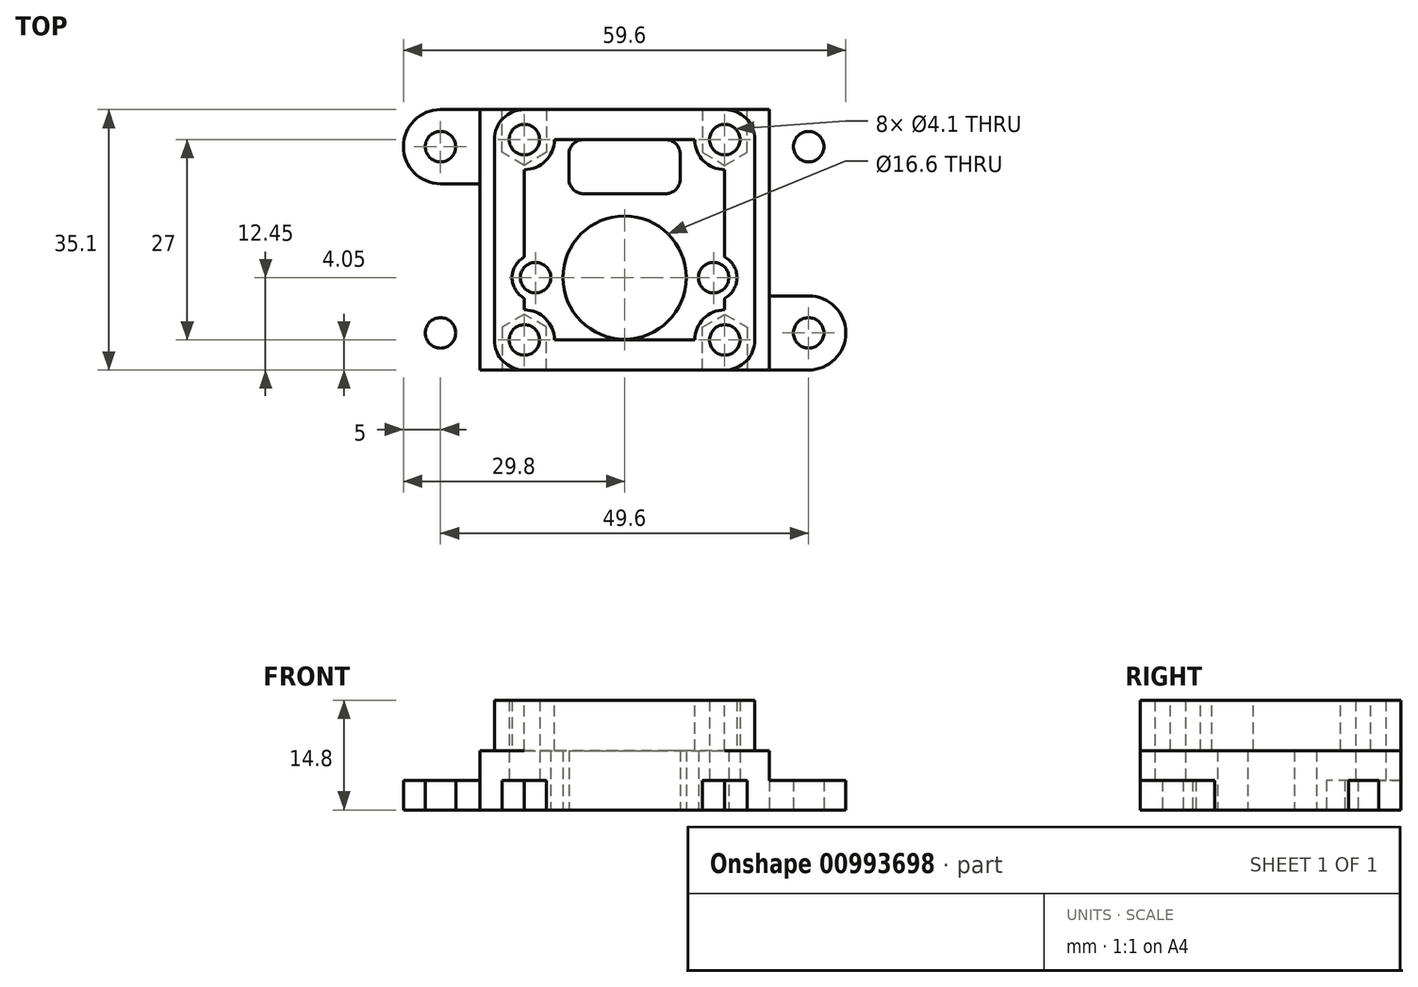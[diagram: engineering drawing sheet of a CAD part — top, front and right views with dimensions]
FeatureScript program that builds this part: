
annotation { "Feature Type Name" : "Feature", "Feature Type Description" : "" }
export const myFeature = defineFeature(function(context is Context, id is Id, definition is map)
    precondition{}
    {
        {
            var Q0;
            Q0=qCreatedBy(makeId("Top.planeOp"),FACE);
            var sketch = newSketch(context, id + "F0", { "sketchPlane" : qUnion([Q0])});
            skLineSegment(sketch, "E0.bottom", {"start": v(17.55, 17.55) * mm, "end": v(-17.55, 17.55) * mm});
            skLineSegment(sketch, "E0.top", {"start": v(17.55, -17.55) * mm, "end": v(-17.55, -17.55) * mm});
            skLineSegment(sketch, "E0.left", {"start": v(17.55, 17.55) * mm, "end": v(17.55, -17.55) * mm, "construction": true});
            skLineSegment(sketch, "E0.right", {"start": v(-17.55, 17.55) * mm, "end": v(-17.55, -17.55) * mm, "construction": true});
            skPoint(sketch, "E0.middle", {"position": v(0, 0) * mm});
            skLineSegment(sketch, "E1", {"start": v(0, 0) * mm, "end": v(0, 17.55) * mm, "construction": true});
            skLineSegment(sketch, "E2", {"start": v(0, 0) * mm, "end": v(-17.55, 0) * mm, "construction": true});
            skLineSegment(sketch, "E3.bottom", {"start": v(13.5, 13.5) * mm, "end": v(-13.5, 13.5) * mm});
            skLineSegment(sketch, "E3.top", {"start": v(13.5, -13.5) * mm, "end": v(-13.5, -13.5) * mm});
            skLineSegment(sketch, "E3.left", {"start": v(13.5, 13.5) * mm, "end": v(13.5, -13.5) * mm});
            skLineSegment(sketch, "E3.right", {"start": v(-13.5, 13.5) * mm, "end": v(-13.5, -13.5) * mm});
            skCircle(sketch, "E4", {"center": v(-13.5, 13.5) * mm, "radius": 2.05 * mm});
            skCircle(sketch, "E5", {"center": v(-13.5, 13.5) * mm, "radius": 4.05 * mm, "construction": true});
            skCircle(sketch, "E6.MirrorC", {"center": v(13.5, 13.5) * mm, "radius": 4.05 * mm, "construction": true});
            skCircle(sketch, "E7.MirrorC", {"center": v(13.5, 13.5) * mm, "radius": 2.05 * mm});
            skCircle(sketch, "E8.MirrorC", {"center": v(-13.5, -13.5) * mm, "radius": 4.05 * mm, "construction": true});
            skCircle(sketch, "E9.MirrorC", {"center": v(-13.5, -13.5) * mm, "radius": 2.05 * mm});
            skCircle(sketch, "E10.MirrorC", {"center": v(13.5, -13.5) * mm, "radius": 4.05 * mm, "construction": true});
            skCircle(sketch, "E11.MirrorC", {"center": v(13.5, -13.5) * mm, "radius": 2.05 * mm});
            skLineSegment(sketch, "E12", {"start": v(-17.55, 17.55) * mm, "end": v(-19.5, 17.55) * mm});
            skLineSegment(sketch, "E13", {"start": v(-19.5, -17.55) * mm, "end": v(-17.55, -17.55) * mm});
            skLineSegment(sketch, "E14.MirrorCS", {"start": v(17.55, 17.55) * mm, "end": v(19.5, 17.55) * mm});
            skLineSegment(sketch, "E15.MirrorCS", {"start": v(19.5, -17.55) * mm, "end": v(17.55, -17.55) * mm});
            skCircle(sketch, "E16", {"center": v(-24.8, 12.55) * mm, "radius": 2.05 * mm});
            skCircle(sketch, "E17.MirrorC", {"center": v(24.8, 12.55) * mm, "radius": 2.05 * mm});
            skCircle(sketch, "E18.MirrorC", {"center": v(-24.8, -12.55) * mm, "radius": 2.05 * mm});
            skCircle(sketch, "E19.MirrorC", {"center": v(24.8, -12.55) * mm, "radius": 2.05 * mm});
            skCircle(sketch, "E20.cCircle", {"center": v(-13.5, 13.5) * mm, "radius": 3 * mm, "construction": true});
            skLineSegment(sketch, "E20.0", {"start": v(-10.5, 15.23) * mm, "end": v(-10.5, 11.77) * mm});
            skLineSegment(sketch, "E20.1", {"start": v(-10.5, 11.77) * mm, "end": v(-13.5, 10.04) * mm});
            skLineSegment(sketch, "E20.2", {"start": v(-13.5, 10.04) * mm, "end": v(-16.5, 11.77) * mm});
            skLineSegment(sketch, "E20.3", {"start": v(-16.5, 11.77) * mm, "end": v(-16.5, 15.23) * mm});
            skLineSegment(sketch, "E20.4", {"start": v(-16.5, 15.23) * mm, "end": v(-13.5, 16.96) * mm});
            skLineSegment(sketch, "E20.5", {"start": v(-13.5, 16.96) * mm, "end": v(-10.5, 15.23) * mm});
            skPoint(sketch, "E20.0.midPoint", {"position": v(-10.5, 13.5) * mm});
            skLineSegment(sketch, "E21.MirrorCS", {"start": v(10.5, 15.23) * mm, "end": v(10.5, 11.77) * mm});
            skLineSegment(sketch, "E22.MirrorCS", {"start": v(13.5, 16.96) * mm, "end": v(10.5, 15.23) * mm});
            skLineSegment(sketch, "E23.MirrorCS", {"start": v(16.5, 15.23) * mm, "end": v(13.5, 16.96) * mm});
            skLineSegment(sketch, "E24.MirrorCS", {"start": v(16.5, 11.77) * mm, "end": v(16.5, 15.23) * mm});
            skLineSegment(sketch, "E25.MirrorCS", {"start": v(13.5, 10.04) * mm, "end": v(16.5, 11.77) * mm});
            skLineSegment(sketch, "E26.MirrorCS", {"start": v(10.5, 11.77) * mm, "end": v(13.5, 10.04) * mm});
            skLineSegment(sketch, "E27.MirrorCS", {"start": v(-10.5, -11.77) * mm, "end": v(-13.5, -10.04) * mm});
            skLineSegment(sketch, "E28.MirrorCS", {"start": v(-10.5, -15.23) * mm, "end": v(-10.5, -11.77) * mm});
            skLineSegment(sketch, "E29.MirrorCS", {"start": v(-13.5, -16.96) * mm, "end": v(-10.5, -15.23) * mm});
            skLineSegment(sketch, "E30.MirrorCS", {"start": v(-16.5, -15.23) * mm, "end": v(-13.5, -16.96) * mm});
            skLineSegment(sketch, "E31.MirrorCS", {"start": v(-16.5, -11.77) * mm, "end": v(-16.5, -15.23) * mm});
            skLineSegment(sketch, "E32.MirrorCS", {"start": v(-13.5, -10.04) * mm, "end": v(-16.5, -11.77) * mm});
            skLineSegment(sketch, "E33.MirrorCS", {"start": v(10.5, -11.77) * mm, "end": v(13.5, -10.04) * mm});
            skLineSegment(sketch, "E34.MirrorCS", {"start": v(10.5, -15.23) * mm, "end": v(10.5, -11.77) * mm});
            skLineSegment(sketch, "E35.MirrorCS", {"start": v(13.5, -16.96) * mm, "end": v(10.5, -15.23) * mm});
            skLineSegment(sketch, "E36.MirrorCS", {"start": v(16.5, -15.23) * mm, "end": v(13.5, -16.96) * mm});
            skLineSegment(sketch, "E37.MirrorCS", {"start": v(16.5, -11.77) * mm, "end": v(16.5, -15.23) * mm});
            skLineSegment(sketch, "E38.MirrorCS", {"start": v(13.5, -10.04) * mm, "end": v(16.5, -11.77) * mm});
            skLineSegment(sketch, "E39", {"start": v(-16.5, 15.23) * mm, "end": v(-16.5, 17.55) * mm});
            skLineSegment(sketch, "E40", {"start": v(-10.5, 15.23) * mm, "end": v(-10.5, 17.55) * mm});
            skLineSegment(sketch, "E41", {"start": v(10.5, 15.23) * mm, "end": v(10.5, 17.55) * mm});
            skLineSegment(sketch, "E42", {"start": v(16.5, 15.23) * mm, "end": v(16.5, 17.55) * mm});
            skLineSegment(sketch, "E43", {"start": v(16.5, -15.23) * mm, "end": v(16.5, -17.55) * mm});
            skLineSegment(sketch, "E44", {"start": v(10.5, -15.23) * mm, "end": v(10.5, -17.55) * mm});
            skLineSegment(sketch, "E45", {"start": v(-10.5, -15.23) * mm, "end": v(-10.5, -17.55) * mm});
            skLineSegment(sketch, "E46", {"start": v(-16.5, -15.23) * mm, "end": v(-16.5, -17.55) * mm});
            skLineSegment(sketch, "E47", {"start": v(-19.5, 17.55) * mm, "end": v(-19.5, -17.55) * mm});
            skLineSegment(sketch, "E48", {"start": v(19.5, 17.55) * mm, "end": v(19.5, -17.55) * mm});
            skCircle(sketch, "E49", {"center": v(0, -5.1) * mm, "radius": 8.3 * mm});
            skCircle(sketch, "E50", {"center": v(-12, -5.1) * mm, "radius": 2.05 * mm});
            skCircle(sketch, "E51", {"center": v(-12, -5.1) * mm, "radius": 3.15 * mm});
            skLineSegment(sketch, "E52", {"start": v(-13.5, -5.1) * mm, "end": v(13.5, -5.1) * mm, "construction": true});
            skLineSegment(sketch, "E53.bottom", {"start": v(-5.5, 13.5) * mm, "end": v(5.5, 13.5) * mm});
            skLineSegment(sketch, "E53.top", {"start": v(-5.5, 6.2) * mm, "end": v(5.5, 6.2) * mm});
            skLineSegment(sketch, "E53.left", {"start": v(-7.5, 11.5) * mm, "end": v(-7.5, 8.2) * mm});
            skLineSegment(sketch, "E53.right", {"start": v(7.5, 11.5) * mm, "end": v(7.5, 8.2) * mm});
            skPoint(sketch, "E53.middle", {"position": v(0, 9.85) * mm});
            skPoint(sketch, "E54.visualSharp", {"position": v(-7.5, 6.2) * mm});
            skArc(sketch, "E54.filletArc", {"start": v(-7.5, 8.2) * mm, "mid": v(-6.91, 6.79) * mm, "end": v(-5.5, 6.2) * mm});
            skPoint(sketch, "E55.visualSharp", {"position": v(7.5, 6.2) * mm});
            skArc(sketch, "E55.filletArc", {"start": v(5.5, 6.2) * mm, "mid": v(6.91, 6.79) * mm, "end": v(7.5, 8.2) * mm});
            skPoint(sketch, "E56.visualSharp", {"position": v(7.5, 13.5) * mm});
            skArc(sketch, "E56.filletArc", {"start": v(7.5, 11.5) * mm, "mid": v(6.91, 12.91) * mm, "end": v(5.5, 13.5) * mm});
            skPoint(sketch, "E57.visualSharp", {"position": v(-7.5, 13.5) * mm});
            skArc(sketch, "E57.filletArc", {"start": v(-5.5, 13.5) * mm, "mid": v(-6.91, 12.91) * mm, "end": v(-7.5, 11.5) * mm});
            skArc(sketch, "E58", {"start": v(-24.8, 17.55) * mm, "mid": v(-29.8, 12.55) * mm, "end": v(-24.8, 7.55) * mm});
            skArc(sketch, "E59", {"start": v(-24.8, -7.55) * mm, "mid": v(-29.8, -12.55) * mm, "end": v(-24.8, -17.55) * mm});
            skLineSegment(sketch, "E60", {"start": v(-24.8, 17.55) * mm, "end": v(-19.5, 17.55) * mm});
            skLineSegment(sketch, "E61", {"start": v(-24.8, 7.55) * mm, "end": v(-19.5, 7.55) * mm});
            skLineSegment(sketch, "E62.MirrorCS", {"start": v(24.8, 7.55) * mm, "end": v(19.5, 7.55) * mm});
            skArc(sketch, "E63.MirrorCS", {"start": v(24.8, 17.55) * mm, "mid": v(29.8, 12.55) * mm, "end": v(24.8, 7.55) * mm});
            skLineSegment(sketch, "E64.MirrorCS", {"start": v(24.8, 17.55) * mm, "end": v(19.5, 17.55) * mm});
            skLineSegment(sketch, "E65.MirrorCS", {"start": v(-24.8, -7.55) * mm, "end": v(-19.5, -7.55) * mm});
            skArc(sketch, "E66.MirrorCS", {"start": v(-24.8, -17.55) * mm, "mid": v(-29.8, -12.55) * mm, "end": v(-24.8, -7.55) * mm});
            skLineSegment(sketch, "E67.MirrorCS", {"start": v(-24.8, -17.55) * mm, "end": v(-19.5, -17.55) * mm});
            skLineSegment(sketch, "E68.MirrorCS", {"start": v(24.8, -17.55) * mm, "end": v(19.5, -17.55) * mm});
            skArc(sketch, "E69.MirrorCS", {"start": v(24.8, -17.55) * mm, "mid": v(29.8, -12.55) * mm, "end": v(24.8, -7.55) * mm});
            skLineSegment(sketch, "E70.MirrorCS", {"start": v(24.8, -7.55) * mm, "end": v(19.5, -7.55) * mm});
            skCircle(sketch, "E71.MirrorC", {"center": v(12, -5.1) * mm, "radius": 3.15 * mm});
            skCircle(sketch, "E72.MirrorC", {"center": v(12, -5.1) * mm, "radius": 2.05 * mm});
            skSolve(sketch);
        }
        {
            var Q0;
            {var subQ1=sQuery(id+"F0.wireOp",EDGE,"E20.2");Q0=makeQuery(id+"F0.imprint","IMPRINT",FACE,{"disambiguationData":[TD([[makeQuery(id+"F0.imprint","IMPRINT",EDGE,{"derivedFrom":subQ1}),1.0]])]});}
            var Q1;
            {var subQ1=sQuery(id+"F0.wireOp",EDGE,"E20.1");Q1=makeQuery(id+"F0.imprint","IMPRINT",FACE,{"disambiguationData":[TD([[makeQuery(id+"F0.imprint","IMPRINT",EDGE,{"derivedFrom":subQ1}),1.0]])]});}
            var Q2;
            {var subQ0=sQuery(id+"F0.wireOp",EDGE,"E40");Q2=makeQuery(id+"F0.imprint","IMPRINT",FACE,{"disambiguationData":[TD([[makeQuery(id+"F0.imprint","IMPRINT",EDGE,{"derivedFrom":subQ0}),-1.0]])]});}
            var Q3;
            Q3=makeQuery(id+"F0.imprint","IMPRINT",FACE,{"disambiguationData":[TD([[makeQuery(id+"F0.imprint","IMPRINT",EDGE,{"derivedFrom":sQuery(id+"F0.wireOp",EDGE,"E24.MirrorCS")}),-1.0]])]});
            var Q4;
            {var subQ7=sQuery(id+"F0.wireOp",EDGE,"E44");Q4=makeQuery(id+"F0.imprint","IMPRINT",FACE,{"disambiguationData":[TD([[makeQuery(id+"F0.imprint","IMPRINT",EDGE,{"derivedFrom":subQ7}),-1.0]])]});}
            var Q5;
            Q5=makeQuery(id+"F0.imprint","IMPRINT",FACE,{"disambiguationData":[TD([[makeQuery(id+"F0.imprint","IMPRINT",EDGE,{"derivedFrom":sQuery(id+"F0.wireOp",EDGE,"E20.4")}),1.0]])]});
            var Q6;
            {var subQ8=sQuery(id+"F0.wireOp",EDGE,"E20.2");Q6=makeQuery(id+"F0.imprint","IMPRINT",FACE,{"disambiguationData":[TD([[makeQuery(id+"F0.imprint","IMPRINT",EDGE,{"derivedFrom":subQ8}),-1.0]])]});}
            var Q7;
            Q7=makeQuery(id+"F0.imprint","IMPRINT",FACE,{"disambiguationData":[TD([[makeQuery(id+"F0.imprint","IMPRINT",EDGE,{"derivedFrom":sQuery(id+"F0.wireOp",EDGE,"E22.MirrorCS")}),-1.0]])]});
            var Q8;
            {var subQ6=sQuery(id+"F0.wireOp",EDGE,"E22.MirrorCS");Q8=makeQuery(id+"F0.imprint","IMPRINT",FACE,{"disambiguationData":[TD([[makeQuery(id+"F0.imprint","IMPRINT",EDGE,{"derivedFrom":subQ6}),1.0]])]});}
            var Q9;
            {var subQ0=sQuery(id+"F0.wireOp",EDGE,"E26.MirrorCS");Q9=makeQuery(id+"F0.imprint","IMPRINT",FACE,{"disambiguationData":[TD([[makeQuery(id+"F0.imprint","IMPRINT",EDGE,{"derivedFrom":subQ0}),1.0]])]});}
            var Q10;
            {var subQ0=sQuery(id+"F0.wireOp",EDGE,"E20.1");Q10=makeQuery(id+"F0.imprint","IMPRINT",FACE,{"disambiguationData":[TD([[makeQuery(id+"F0.imprint","IMPRINT",EDGE,{"derivedFrom":subQ0}),-1.0]])]});}
            var Q11;
            {var subQ5=sQuery(id+"F0.wireOp",EDGE,"E27.MirrorCS");Q11=makeQuery(id+"F0.imprint","IMPRINT",FACE,{"disambiguationData":[TD([[makeQuery(id+"F0.imprint","IMPRINT",EDGE,{"derivedFrom":subQ5}),1.0]])]});}
            var Q12;
            {var subQ0=sQuery(id+"F0.wireOp",EDGE,"E29.MirrorCS");Q12=makeQuery(id+"F0.imprint","IMPRINT",FACE,{"disambiguationData":[TD([[makeQuery(id+"F0.imprint","IMPRINT",EDGE,{"derivedFrom":subQ0}),1.0]])]});}
            var Q13;
            Q13=makeQuery(id+"F0.imprint","IMPRINT",FACE,{"disambiguationData":[TD([[makeQuery(id+"F0.imprint","IMPRINT",EDGE,{"derivedFrom":sQuery(id+"F0.wireOp",EDGE,"E29.MirrorCS")}),-1.0]])]});
            var Q14;
            Q14=makeQuery(id+"F0.imprint","IMPRINT",FACE,{"disambiguationData":[TD([[makeQuery(id+"F0.imprint","IMPRINT",EDGE,{"derivedFrom":sQuery(id+"F0.wireOp",EDGE,"E35.MirrorCS")}),1.0]])]});
            var Q15;
            {var subQ0=sQuery(id+"F0.wireOp",EDGE,"E35.MirrorCS");Q15=makeQuery(id+"F0.imprint","IMPRINT",FACE,{"disambiguationData":[TD([[makeQuery(id+"F0.imprint","IMPRINT",EDGE,{"derivedFrom":subQ0}),-1.0]])]});}
            var Q16;
            {var subQ7=sQuery(id+"F0.wireOp",EDGE,"E33.MirrorCS");Q16=makeQuery(id+"F0.imprint","IMPRINT",FACE,{"disambiguationData":[TD([[makeQuery(id+"F0.imprint","IMPRINT",EDGE,{"derivedFrom":subQ7}),-1.0]])]});}
            var Q17;
            Q17=makeQuery(id+"F0.imprint","IMPRINT",FACE,{"disambiguationData":[TD([[makeQuery(id+"F0.imprint","IMPRINT",EDGE,{"derivedFrom":sQuery(id+"F0.wireOp",EDGE,"nuV7RpCx-R8Kc-sA3T-knKH-8SdXEwqvr1Y3")}),1.0]])]});
            var Q18;
            Q18=makeQuery(id+"F0.imprint","IMPRINT",FACE,{"disambiguationData":[TD([[makeQuery(id+"F0.imprint","IMPRINT",EDGE,{"derivedFrom":sQuery(id+"F0.wireOp",EDGE,"B5VoDuBN-S8xL-bz7c-algA-acrGaq53pSVS")}),1.0]])]});
            var Q19;
            {var subQ7=sQuery(id+"F0.wireOp",EDGE,"B5VoDuBN-S8xL-bz7c-algA-acrGaq53pSVS");Q19=makeQuery(id+"F0.imprint","IMPRINT",FACE,{"disambiguationData":[TD([[makeQuery(id+"F0.imprint","IMPRINT",EDGE,{"derivedFrom":subQ7}),-1.0]])]});}
            var Q20;
            {var subQ0=sQuery(id+"F0.wireOp",EDGE,"E26.MirrorCS");Q20=makeQuery(id+"F0.imprint","IMPRINT",FACE,{"disambiguationData":[TD([[makeQuery(id+"F0.imprint","IMPRINT",EDGE,{"derivedFrom":subQ0}),-1.0]])]});}
            var Q21;
            Q21=makeQuery(id+"F0.imprint","IMPRINT",FACE,{"disambiguationData":[TD([[makeQuery(id+"F0.imprint","IMPRINT",EDGE,{"derivedFrom":sQuery(id+"F0.wireOp",EDGE,"8ItnjwQV-7nQZ-PuKx-0Jwr-2TPdBdbSkfHZ")}),-1.0]])]});
            var Q22;
            Q22=makeQuery(id+"F0.imprint","IMPRINT",FACE,{"disambiguationData":[TD([[makeQuery(id+"F0.imprint","IMPRINT",EDGE,{"derivedFrom":sQuery(id+"F0.wireOp",EDGE,"8adYv2pj-t3p7-Cn0L-WwMu-koROzQhryOGd")}),-1.0]])]});
            var Q23;
            {var subQ0=sQuery(id+"F0.wireOp",EDGE,"wJV0zkYp-PxIc-I7u3-SHVp-S6dmDnbKQt5D");var subQ1=sQuery(id+"F0.wireOp",EDGE,"E3.left");var subQ2=makeQuery(id+"F0.imprint","INTERSECT",VERTEX,{"disambiguationData":[OD(0.0)],"derivedFrom":[subQ1,subQ0]});Q23=makeQuery(id+"F0.imprint","IMPRINT",FACE,{"disambiguationData":[TD([[makeQuery(id+"F0.imprint","IMPRINT",EDGE,{"disambiguationData":[TD([[subQ2,-1.0]])],"derivedFrom":subQ1}),1.0]])]});}
            var Q24;
            Q24=makeQuery(id+"F0.imprint","IMPRINT",FACE,{"disambiguationData":[TD([[makeQuery(id+"F0.imprint","IMPRINT",EDGE,{"derivedFrom":sQuery(id+"F0.wireOp",EDGE,"8ItnjwQV-7nQZ-PuKx-0Jwr-2TPdBdbSkfHZ")}),1.0]])]});
            var Q25;
            {var subQ0=sQuery(id+"F0.wireOp",EDGE,"YWPBbz1K-cqDX-BCyH-acbg-6dvT2AnOIS1P");var subQ1=sQuery(id+"F0.wireOp",EDGE,"E3.right");var subQ2=makeQuery(id+"F0.imprint","INTERSECT",VERTEX,{"disambiguationData":[OD(0.0)],"derivedFrom":[subQ1,subQ0]});Q25=makeQuery(id+"F0.imprint","IMPRINT",FACE,{"disambiguationData":[TD([[makeQuery(id+"F0.imprint","IMPRINT",EDGE,{"disambiguationData":[TD([[subQ2,-1.0]])],"derivedFrom":subQ1}),-1.0]])]});}
            var Q26;
            Q26=makeQuery(id+"F0.imprint","IMPRINT",FACE,{"disambiguationData":[TD([[makeQuery(id+"F0.imprint","IMPRINT",EDGE,{"derivedFrom":sQuery(id+"F0.wireOp",EDGE,"8adYv2pj-t3p7-Cn0L-WwMu-koROzQhryOGd")}),1.0]])]});
            extrude(context, id + "F1", {"entities" : qUnion([Q0, Q1, Q2, Q3, Q4, Q5, Q6, Q7, Q8, Q9, Q10, Q11, Q12, Q13, Q14, Q15, Q16, Q17, Q18, Q19, Q20, Q21, Q22, Q23, Q24, Q25, Q26]), "depth" : 14.8 * mm, "offsetDistance" : 25 * mm});
        }
        {
            var Q0;
            Q0=makeQuery(id+"F0.imprint","IMPRINT",FACE,{"disambiguationData":[TD([[makeQuery(id+"F0.imprint","IMPRINT",EDGE,{"derivedFrom":sQuery(id+"F0.wireOp",EDGE,"E16")}),-1.0]])]});
            var Q1;
            Q1=makeQuery(id+"F0.imprint","IMPRINT",FACE,{"disambiguationData":[TD([[makeQuery(id+"F0.imprint","IMPRINT",EDGE,{"derivedFrom":sQuery(id+"F0.wireOp",EDGE,"E18.MirrorC")}),1.0]])]});
            var Q2;
            Q2=makeQuery(id+"F0.imprint","IMPRINT",FACE,{"disambiguationData":[TD([[makeQuery(id+"F0.imprint","IMPRINT",EDGE,{"derivedFrom":sQuery(id+"F0.wireOp",EDGE,"E19.MirrorC")}),-1.0]])]});
            var Q3;
            Q3=makeQuery(id+"F0.imprint","IMPRINT",FACE,{"disambiguationData":[TD([[makeQuery(id+"F0.imprint","IMPRINT",EDGE,{"derivedFrom":sQuery(id+"F0.wireOp",EDGE,"E17.MirrorC")}),1.0]])]});
            extrude(context, id + "F2", {"entities" : qUnion([Q0, Q1, Q2, Q3]), "operationType" : NewBodyOperationType.ADD, "depth" : 4 * mm, "offsetDistance" : 25 * mm});
        }
        {
            var Q0;
            {var subQ6=sQuery(id+"F0.wireOp",EDGE,"E22.MirrorCS");Q0=makeQuery(id+"F0.imprint","IMPRINT",FACE,{"disambiguationData":[TD([[makeQuery(id+"F0.imprint","IMPRINT",EDGE,{"derivedFrom":subQ6}),1.0]])]});}
            var Q1;
            {var subQ0=sQuery(id+"F0.wireOp",EDGE,"E26.MirrorCS");Q1=makeQuery(id+"F0.imprint","IMPRINT",FACE,{"disambiguationData":[TD([[makeQuery(id+"F0.imprint","IMPRINT",EDGE,{"derivedFrom":subQ0}),1.0]])]});}
            var Q2;
            Q2=makeQuery(id+"F0.imprint","IMPRINT",FACE,{"disambiguationData":[TD([[makeQuery(id+"F0.imprint","IMPRINT",EDGE,{"derivedFrom":sQuery(id+"F0.wireOp",EDGE,"E22.MirrorCS")}),-1.0]])]});
            var Q3;
            {var subQ8=sQuery(id+"F0.wireOp",EDGE,"E20.2");Q3=makeQuery(id+"F0.imprint","IMPRINT",FACE,{"disambiguationData":[TD([[makeQuery(id+"F0.imprint","IMPRINT",EDGE,{"derivedFrom":subQ8}),-1.0]])]});}
            var Q4;
            {var subQ0=sQuery(id+"F0.wireOp",EDGE,"E20.1");Q4=makeQuery(id+"F0.imprint","IMPRINT",FACE,{"disambiguationData":[TD([[makeQuery(id+"F0.imprint","IMPRINT",EDGE,{"derivedFrom":subQ0}),-1.0]])]});}
            var Q5;
            Q5=makeQuery(id+"F0.imprint","IMPRINT",FACE,{"disambiguationData":[TD([[makeQuery(id+"F0.imprint","IMPRINT",EDGE,{"derivedFrom":sQuery(id+"F0.wireOp",EDGE,"E20.4")}),1.0]])]});
            var Q6;
            {var subQ7=sQuery(id+"F0.wireOp",EDGE,"E33.MirrorCS");Q6=makeQuery(id+"F0.imprint","IMPRINT",FACE,{"disambiguationData":[TD([[makeQuery(id+"F0.imprint","IMPRINT",EDGE,{"derivedFrom":subQ7}),-1.0]])]});}
            var Q7;
            {var subQ0=sQuery(id+"F0.wireOp",EDGE,"E35.MirrorCS");Q7=makeQuery(id+"F0.imprint","IMPRINT",FACE,{"disambiguationData":[TD([[makeQuery(id+"F0.imprint","IMPRINT",EDGE,{"derivedFrom":subQ0}),-1.0]])]});}
            var Q8;
            Q8=makeQuery(id+"F0.imprint","IMPRINT",FACE,{"disambiguationData":[TD([[makeQuery(id+"F0.imprint","IMPRINT",EDGE,{"derivedFrom":sQuery(id+"F0.wireOp",EDGE,"E35.MirrorCS")}),1.0]])]});
            var Q9;
            {var subQ0=sQuery(id+"F0.wireOp",EDGE,"E29.MirrorCS");Q9=makeQuery(id+"F0.imprint","IMPRINT",FACE,{"disambiguationData":[TD([[makeQuery(id+"F0.imprint","IMPRINT",EDGE,{"derivedFrom":subQ0}),1.0]])]});}
            var Q10;
            {var subQ5=sQuery(id+"F0.wireOp",EDGE,"E27.MirrorCS");Q10=makeQuery(id+"F0.imprint","IMPRINT",FACE,{"disambiguationData":[TD([[makeQuery(id+"F0.imprint","IMPRINT",EDGE,{"derivedFrom":subQ5}),1.0]])]});}
            var Q11;
            Q11=makeQuery(id+"F0.imprint","IMPRINT",FACE,{"disambiguationData":[TD([[makeQuery(id+"F0.imprint","IMPRINT",EDGE,{"derivedFrom":sQuery(id+"F0.wireOp",EDGE,"E29.MirrorCS")}),-1.0]])]});
            extrude(context, id + "F3", {"entities" : qUnion([Q0, Q1, Q2, Q3, Q4, Q5, Q6, Q7, Q8, Q9, Q10, Q11]), "operationType" : NewBodyOperationType.REMOVE, "depth" : 4 * mm, "offsetDistance" : 25 * mm});
        }
        {
            var Q0;
            Q0=makeQuery(id+"F1.opExtrude","CAP_FACE",FACE,{"disambiguationData":[OSD([sQuery(id+"F0.wireOp",EDGE,"E0.bottom"),sQuery(id+"F0.wireOp",EDGE,"E0.top"),sQuery(id+"F0.wireOp",EDGE,"E4"),sQuery(id+"F0.wireOp",EDGE,"E7.MirrorC"),sQuery(id+"F0.wireOp",EDGE,"E9.MirrorC"),sQuery(id+"F0.wireOp",EDGE,"E11.MirrorC"),sQuery(id+"F0.wireOp",EDGE,"E12"),sQuery(id+"F0.wireOp",EDGE,"E13"),sQuery(id+"F0.wireOp",EDGE,"E14.MirrorCS"),sQuery(id+"F0.wireOp",EDGE,"E15.MirrorCS"),sQuery(id+"F0.wireOp",EDGE,"nuV7RpCx-R8Kc-sA3T-knKH-8SdXEwqvr1Y3"),sQuery(id+"F0.wireOp",EDGE,"B5VoDuBN-S8xL-bz7c-algA-acrGaq53pSVS"),sQuery(id+"F0.wireOp",EDGE,"E47"),sQuery(id+"F0.wireOp",EDGE,"E48")])],"isStart":false});
            var sketch = newSketch(context, id + "F4", { "sketchPlane" : qUnion([Q0])});
            skCircle(sketch, "E73.0", {"center": v(13.5, 13.5) * mm, "radius": 2.05 * mm});
            skCircle(sketch, "E73.1", {"center": v(13.5, -13.5) * mm, "radius": 2.05 * mm});
            skCircle(sketch, "E73.2", {"center": v(-13.5, -13.5) * mm, "radius": 2.05 * mm});
            skCircle(sketch, "E73.3", {"center": v(-13.5, 13.5) * mm, "radius": 2.05 * mm});
            skLineSegment(sketch, "E74", {"start": v(13.5, 13.5) * mm, "end": v(-13.5, 13.5) * mm});
            skLineSegment(sketch, "E75", {"start": v(-13.5, -13.5) * mm, "end": v(-13.5, 13.5) * mm});
            skLineSegment(sketch, "E76", {"start": v(-13.5, -13.5) * mm, "end": v(13.5, -13.5) * mm});
            skLineSegment(sketch, "E77", {"start": v(13.5, -13.5) * mm, "end": v(13.5, 13.5) * mm});
            skLineSegment(sketch, "E78.0", {"start": v(19.5, 17.55) * mm, "end": v(-19.5, 17.55) * mm});
            skLineSegment(sketch, "E79.0", {"start": v(-19.5, -17.55) * mm, "end": v(19.5, -17.55) * mm});
            skCircle(sketch, "E80", {"center": v(-13.5, 13.5) * mm, "radius": 4.05 * mm});
            skCircle(sketch, "E81", {"center": v(13.5, 13.5) * mm, "radius": 4.05 * mm});
            skCircle(sketch, "E82", {"center": v(-13.5, -13.5) * mm, "radius": 4.05 * mm});
            skCircle(sketch, "E83", {"center": v(13.5, -13.5) * mm, "radius": 4.05 * mm});
            skLineSegment(sketch, "E84", {"start": v(17.55, -17.55) * mm, "end": v(17.55, 17.55) * mm});
            skLineSegment(sketch, "E85", {"start": v(-17.55, -17.55) * mm, "end": v(-17.55, 17.55) * mm});
            skSolve(sketch);
        }
        {
            var Q0;
            {var subQ0=sQuery(id+"F4.wireOp",EDGE,"E85");var subQ1=sQuery(id+"F4.wireOp",EDGE,"E79.0");var subQ2=makeQuery(id+"F4.imprint","INTERSECT",VERTEX,{"derivedFrom":[subQ1,subQ0]});Q0=makeQuery(id+"F4.imprint","IMPRINT",FACE,{"disambiguationData":[TD([[makeQuery(id+"F4.imprint","IMPRINT",EDGE,{"disambiguationData":[TD([[subQ2,-1.0]])],"derivedFrom":subQ1}),1.0]])]});}
            var Q1;
            {var subQ4=makeQuery(id+"F1.opExtrude","CAP_EDGE",EDGE,{"disambiguationData":[OSD([sQuery(id+"F0.wireOp",EDGE,"E47")])],"isStart":false});Q1=makeQuery(id+"F4.imprint","IMPRINT",FACE,{"disambiguationData":[TD([[makeQuery(id+"F4.imprint","IMPRINT",EDGE,{"derivedFrom":subQ4}),1.0]])]});}
            var Q2;
            {var subQ0=sQuery(id+"F4.wireOp",EDGE,"E85");var subQ1=sQuery(id+"F4.wireOp",EDGE,"E78.0");var subQ2=makeQuery(id+"F4.imprint","INTERSECT",VERTEX,{"derivedFrom":[subQ1,subQ0]});Q2=makeQuery(id+"F4.imprint","IMPRINT",FACE,{"disambiguationData":[TD([[makeQuery(id+"F4.imprint","IMPRINT",EDGE,{"disambiguationData":[TD([[subQ2,1.0]])],"derivedFrom":subQ1}),1.0]])]});}
            var Q3;
            {var subQ0=sQuery(id+"F4.wireOp",EDGE,"E84");var subQ1=sQuery(id+"F4.wireOp",EDGE,"E78.0");var subQ2=makeQuery(id+"F4.imprint","INTERSECT",VERTEX,{"derivedFrom":[subQ1,subQ0]});Q3=makeQuery(id+"F4.imprint","IMPRINT",FACE,{"disambiguationData":[TD([[makeQuery(id+"F4.imprint","IMPRINT",EDGE,{"disambiguationData":[TD([[subQ2,-1.0]])],"derivedFrom":subQ1}),1.0]])]});}
            var Q4;
            {var subQ5=makeQuery(id+"F1.opExtrude","CAP_EDGE",EDGE,{"disambiguationData":[OSD([sQuery(id+"F0.wireOp",EDGE,"E48")])],"isStart":false});Q4=makeQuery(id+"F4.imprint","IMPRINT",FACE,{"disambiguationData":[TD([[makeQuery(id+"F4.imprint","IMPRINT",EDGE,{"derivedFrom":subQ5}),-1.0]])]});}
            var Q5;
            {var subQ0=sQuery(id+"F4.wireOp",EDGE,"E84");var subQ1=sQuery(id+"F4.wireOp",EDGE,"E79.0");var subQ2=makeQuery(id+"F4.imprint","INTERSECT",VERTEX,{"derivedFrom":[subQ1,subQ0]});Q5=makeQuery(id+"F4.imprint","IMPRINT",FACE,{"disambiguationData":[TD([[makeQuery(id+"F4.imprint","IMPRINT",EDGE,{"disambiguationData":[TD([[subQ2,1.0]])],"derivedFrom":subQ1}),1.0]])]});}
            var Q6;
            Q6=makeQuery(id+"F4.imprint","IMPRINT",FACE,{"disambiguationData":[TD([[makeQuery(id+"F4.imprint","IMPRINT",EDGE,{"derivedFrom":makeQuery(id+"F1.opExtrude","CAP_EDGE",EDGE,{"disambiguationData":[OSD([sQuery(id+"F0.wireOp",EDGE,"nuV7RpCx-R8Kc-sA3T-knKH-8SdXEwqvr1Y3")])],"isStart":false})}),1.0]])]});
            var Q7;
            {var subQ17=makeQuery(id+"F1.opExtrude","CAP_EDGE",EDGE,{"disambiguationData":[OSD([sQuery(id+"F0.wireOp",EDGE,"E49")])],"isStart":false});Q7=makeQuery(id+"F4.imprint","IMPRINT",FACE,{"disambiguationData":[TD([[makeQuery(id+"F4.imprint","IMPRINT",EDGE,{"derivedFrom":subQ17}),-1.0]])]});}
            extrude(context, id + "F5", {"entities" : qUnion([Q0, Q1, Q2, Q3, Q4, Q5, Q6, Q7]), "operationType" : NewBodyOperationType.REMOVE, "oppositeDirection" : true, "depth" : (14.8 - 4 - 4) * mm, "offsetDistance" : 25 * mm});
        }
        {
            var Q0;
            {var subQ0=sQuery(id+"F0.wireOp",EDGE,"E51");var subQ1=sQuery(id+"F0.wireOp",EDGE,"E3.right");var subQ2=makeQuery(id+"F0.imprint","INTERSECT",VERTEX,{"disambiguationData":[OD(0.0)],"derivedFrom":[subQ1,subQ0]});Q0=makeQuery(id+"F0.imprint","IMPRINT",FACE,{"disambiguationData":[TD([[makeQuery(id+"F0.imprint","IMPRINT",EDGE,{"disambiguationData":[TD([[subQ2,-1.0]])],"derivedFrom":subQ1}),1.0]])]});}
            var Q1;
            {var subQ0=sQuery(id+"F0.wireOp",EDGE,"zwe8mHyR-mkQM-F6wM-OGqH-OivxLTibEfLd");var subQ1=sQuery(id+"F0.wireOp",EDGE,"E3.left");var subQ2=makeQuery(id+"F0.imprint","INTERSECT",VERTEX,{"disambiguationData":[OD(0.0)],"derivedFrom":[subQ1,subQ0]});Q1=makeQuery(id+"F0.imprint","IMPRINT",FACE,{"disambiguationData":[TD([[makeQuery(id+"F0.imprint","IMPRINT",EDGE,{"disambiguationData":[TD([[subQ2,-1.0]])],"derivedFrom":subQ1}),1.0]])]});}
            var Q2;
            {var subQ0=sQuery(id+"F0.wireOp",EDGE,"zwe8mHyR-mkQM-F6wM-OGqH-OivxLTibEfLd");var subQ1=sQuery(id+"F0.wireOp",EDGE,"E3.left");var subQ2=makeQuery(id+"F0.imprint","INTERSECT",VERTEX,{"disambiguationData":[OD(0.0)],"derivedFrom":[subQ1,subQ0]});Q2=makeQuery(id+"F0.imprint","IMPRINT",FACE,{"disambiguationData":[TD([[makeQuery(id+"F0.imprint","IMPRINT",EDGE,{"disambiguationData":[TD([[subQ2,-1.0]])],"derivedFrom":subQ1}),-1.0]])]});}
            var Q3;
            {var subQ0=sQuery(id+"F0.wireOp",EDGE,"E51");var subQ1=sQuery(id+"F0.wireOp",EDGE,"E3.right");var subQ2=makeQuery(id+"F0.imprint","INTERSECT",VERTEX,{"disambiguationData":[OD(0.0)],"derivedFrom":[subQ1,subQ0]});Q3=makeQuery(id+"F0.imprint","IMPRINT",FACE,{"disambiguationData":[TD([[makeQuery(id+"F0.imprint","IMPRINT",EDGE,{"disambiguationData":[TD([[subQ2,-1.0]])],"derivedFrom":subQ1}),-1.0]])]});}
            var Q4;
            {var subQ0=sQuery(id+"F0.wireOp",EDGE,"E71.MirrorC");var subQ1=sQuery(id+"F0.wireOp",EDGE,"E3.left");var subQ2=makeQuery(id+"F0.imprint","INTERSECT",VERTEX,{"disambiguationData":[OD(0.0)],"derivedFrom":[subQ1,subQ0]});Q4=makeQuery(id+"F0.imprint","IMPRINT",FACE,{"disambiguationData":[TD([[makeQuery(id+"F0.imprint","IMPRINT",EDGE,{"disambiguationData":[TD([[subQ2,-1.0]])],"derivedFrom":subQ1}),-1.0]])]});}
            var Q5;
            {var subQ0=sQuery(id+"F0.wireOp",EDGE,"E71.MirrorC");var subQ1=sQuery(id+"F0.wireOp",EDGE,"E3.left");var subQ2=makeQuery(id+"F0.imprint","INTERSECT",VERTEX,{"disambiguationData":[OD(0.0)],"derivedFrom":[subQ1,subQ0]});Q5=makeQuery(id+"F0.imprint","IMPRINT",FACE,{"disambiguationData":[TD([[makeQuery(id+"F0.imprint","IMPRINT",EDGE,{"disambiguationData":[TD([[subQ2,-1.0]])],"derivedFrom":subQ1}),1.0]])]});}
            extrude(context, id + "F6", {"entities" : qUnion([Q0, Q1, Q2, Q3, Q4, Q5]), "operationType" : NewBodyOperationType.ADD, "depth" : 8 * mm, "offsetDistance" : 25 * mm});
        }
    });
